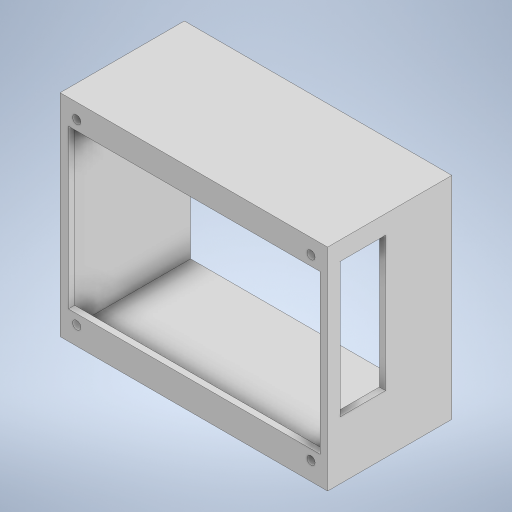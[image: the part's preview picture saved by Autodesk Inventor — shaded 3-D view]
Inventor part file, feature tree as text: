
AUTODESK INVENTOR PART (.ipt)
format: ipt  version: 2023 (Build 270158000, 158)  size: 625,664 bytes
history: native  units: mm
features: extrude x7, sketch x7
ambient origin geometry x8: Origin, YZ Plane, XZ Plane, XY Plane, X Axis, Y Axis, Z Axis, Center Point
bodies: Solid1 (feature_tree)
feature tree (14):
  extrude  "Extrusion1"  Depth=60.0mm
  extrude  "Extrusion2"  Depth=76.4mm
  extrude  "Extrusion4"  Depth=2.0mm
  extrude  "Extrusion6"  Depth=4.0mm
  extrude  "Extrusion7"  Depth=4.0mm
  extrude  "Extrusion8"  Depth=4.0mm
  extrude  "Extrusion9"  Depth=2.0mm
  sketch  "Sketch1"  dims[d0=125.15mm d1=60.0mm]
  sketch  "Sketch2"  dims[d2=100.0mm d3=0.0mm d4=76.4mm]
  sketch  "Sketch5"  dims[d5=121.51mm d7=2.0mm]
  sketch  "Sketch7"  dims[d15=10.0mm d16=4.0mm]
  sketch  "Sketch8"  dims[d17=4.765mm d18=4.0mm]
  sketch  "Sketch9"  dims[d19=85.93mm d21=4.0mm]
  sketch  "Sketch10"  dims[d22=113.11mm d23=6.02mm d24=4.0mm d25=4.765mm d26=113.11mm d27=3.0mm d28=0.0mm d35=7.0mm d37=6.0mm d38=22.0mm d39=65.0mm d40=10.0mm d41=0.0mm d46=1.0mm d47=4.0mm d48=1.0mm d49=1.0mm d50=57.0mm d51=0.0mm d52=2.0mm d53=0.0mm d54=2.0mm d55=0.0mm d56=2.0mm d57=0.0mm d33=0.5mm d34=0.872665mm d36=0.872665mm]
